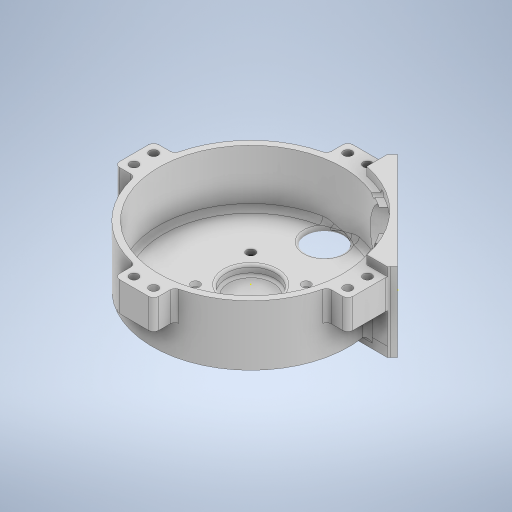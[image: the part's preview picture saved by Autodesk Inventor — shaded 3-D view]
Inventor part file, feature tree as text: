
AUTODESK INVENTOR PART (.ipt)
format: ipt  version: 2023 (Build 270158000, 158)  size: 804,352 bytes
history: native  units: in
note: dims shown in document units (in); Inventor stores cm internally (conversion verified against a paired STEP export)
features: sketch x26, extrude x21, fillet x11, hole x3
ambient origin geometry x8: Origin, YZ Plane, XZ Plane, XY Plane, X Axis, Y Axis, Z Axis, Center Point
bodies: Solid1 (feature_tree)
feature tree (61):
  extrude  "Extrusion1"  Depth=1.375in TaperAngle=0.0deg
  extrude  "Extrusion2"  Depth=1.275in TaperAngle=0.0deg
  extrude  "Extrusion3"  Depth=1.125in TaperAngle=0.0deg
  hole  "Hole1"  [1 undecoded]
  extrude  "Extrusion4"  Depth=0.4in
  extrude  "Extrusion5"  Depth=0.4in
  hole  "Hole2"  [1 undecoded]
  extrude  "Extrusion6"  Depth=0.4in
  sketch  "Sketch10"  dims[d26=0.8in d27=0.4in]
  extrude  "Extrusion7"  Depth=0.4in
  extrude  "Extrusion8"  Depth=0.8in
  extrude  "Extrusion9"  Depth=0.4in
  extrude  "Extrusion18"  Depth=0.75in TaperAngle=0.0deg
  extrude  "Extrusion19"  Depth=0.2in
  extrude  "Extrusion20"  Depth=0.2in
  extrude  "Extrusion21"  Depth=0.4in
  extrude  "Extrusion22"  Depth=0.2in
  extrude  "Extrusion23"  Depth=0.2in
  sketch  "Sketch34"  dims[d125=0.3in d126=0.3in]
  hole  "Hole6"  [1 undecoded]
  extrude  "Extrusion24"  Depth=2.0in TaperAngle=0.0deg
  fillet  "Fillet1"  Radius=2.0in
  fillet  "Fillet2"  Radius=0.3in
  fillet  "Fillet3"  Radius=0.3in
  fillet  "Fillet4"  Radius=0.3in
  fillet  "Fillet5"  Radius=0.3in
  fillet  "Fillet6"  Radius=0.1in
  fillet  "Fillet7"  Radius=0.1in
  fillet  "Fillet8"  Radius=0.175in
  fillet  "Fillet9"  Radius=0.2in
  fillet  "Fillet10"  Radius=1.0875in
  fillet  "Fillet11"  Radius=1.425in
  extrude  "Extrusion25"  Depth=0.5in
  extrude  "Extrusion11"  Depth=0.5in
  extrude  "Extrusion13"  Depth=0.3in
  extrude  "Extrusion14"  Depth=0.3in
  extrude  "Extrusion16"  Depth=1.225in TaperAngle=0.0deg
  sketch  "Sketch1"  dims[d0=4.0in d1=1.375in d2=0.0in]
  sketch  "Sketch2"  dims[d3=3.75in d4=1.275in d5=0.0in]
  sketch  "Sketch3"  dims[d6=1.0in d7=1.125in d8=0.0in]
  sketch  "Sketch4"  dims[d9=1.125in d10=1.125in]
  sketch  "Sketch5"  dims[d11=0.177in d12=0.75in d13=0.332in d14=0.25in d15=0.5635in d16=1.0in d17=0.8108in d18=0.4in]
  sketch  "Sketch6"  dims[d19=0.5in d20=0.4in]
  sketch  "Sketch7"  dims[d21=0.5in d22=0.75in d23=0.0in]
  sketch  "Sketch8"  dims[d24=0.5in d25=0.4in]
  sketch  "Sketch11"  dims[d28=0.5in d29=0.8in]
  sketch  "Sketch12"  dims[d30=0.5in d31=0.4in]
  sketch  "Sketch13"  dims[d32=0.8in d33=0.75in d34=0.0in]
  sketch  "Sketch17"  dims[d35=0.2in d36=0.2in]
  sketch  "Sketch19"  dims[d37=0.4in d38=0.2in]
  sketch  "Sketch20"  dims[d39=0.2in d40=0.4in]
  sketch  "Sketch23"  dims[d41=0.2in d42=0.2in]
  sketch  "Sketch26"  dims[d43=0.2in d44=0.2in]
  sketch  "Sketch27"  dims[d45=0.4in]
  sketch  "Sketch28"  dims[d46=0.177in d47=0.75in d48=0.375in d49=0.25in d50=0.5635in d51=0.75in d52=0.8108in d53=1.5in]
  sketch  "Sketch30"  dims[d54=0.75in d55=0.0in d66=0.15in d67=0.0in d68=2.0in d69=0.3in d70=0.3in d71=0.3in d72=0.3in d73=0.1in d74=0.0in d75=0.1in d76=0.0in d79=0.175in d80=0.0in d84=0.2in d85=0.0in d86=1.0875in d87=0.0in d101=1.425in d102=0.0in]
  sketch  "Sketch32"  dims[d105=0.3in d106=0.0in d122=0.5in]
  sketch  "Sketch33"  dims[d123=0.5in d124=0.5in]
  sketch  "Sketch35"  dims[d127=0.3in d128=0.3in]
  sketch  "Sketch36"  dims[d129=0.175in d130=1.225in d131=0.0in d132=0.0in d133=0.0625in d134=1.125in d135=0.0in d136=0.0in]
  sketch  "Sketch37"  dims[d137=0.15in d138=1.6in d139=0.0in d140=0.375in d141=0.0in d142=0.2in d143=0.0in d144=0.3in d145=0.2in d146=0.0in d147=0.8in d148=1.275in d149=1.275in d150=0.126in d151=0.75in d152=0.248in d153=0.25in d154=90.0deg d155=0.5in d156=0.8108in d157=1.5in d158=0.4in d159=0.0in d160=0.25in d161=0.25in d162=0.25in d163=0.1in d164=0.1in d165=0.1in d166=0.1in d167=0.05in d168=0.05in d169=0.1in d170=0.1in d171=0.175in d172=0.0in d81=0.5in d82=0.0344in]
note: 3 required parameter values undecoded (feature->parameter linkage not recoverable at this tier; creation-order binding heuristic only, values carry confidence <= 0.55)
